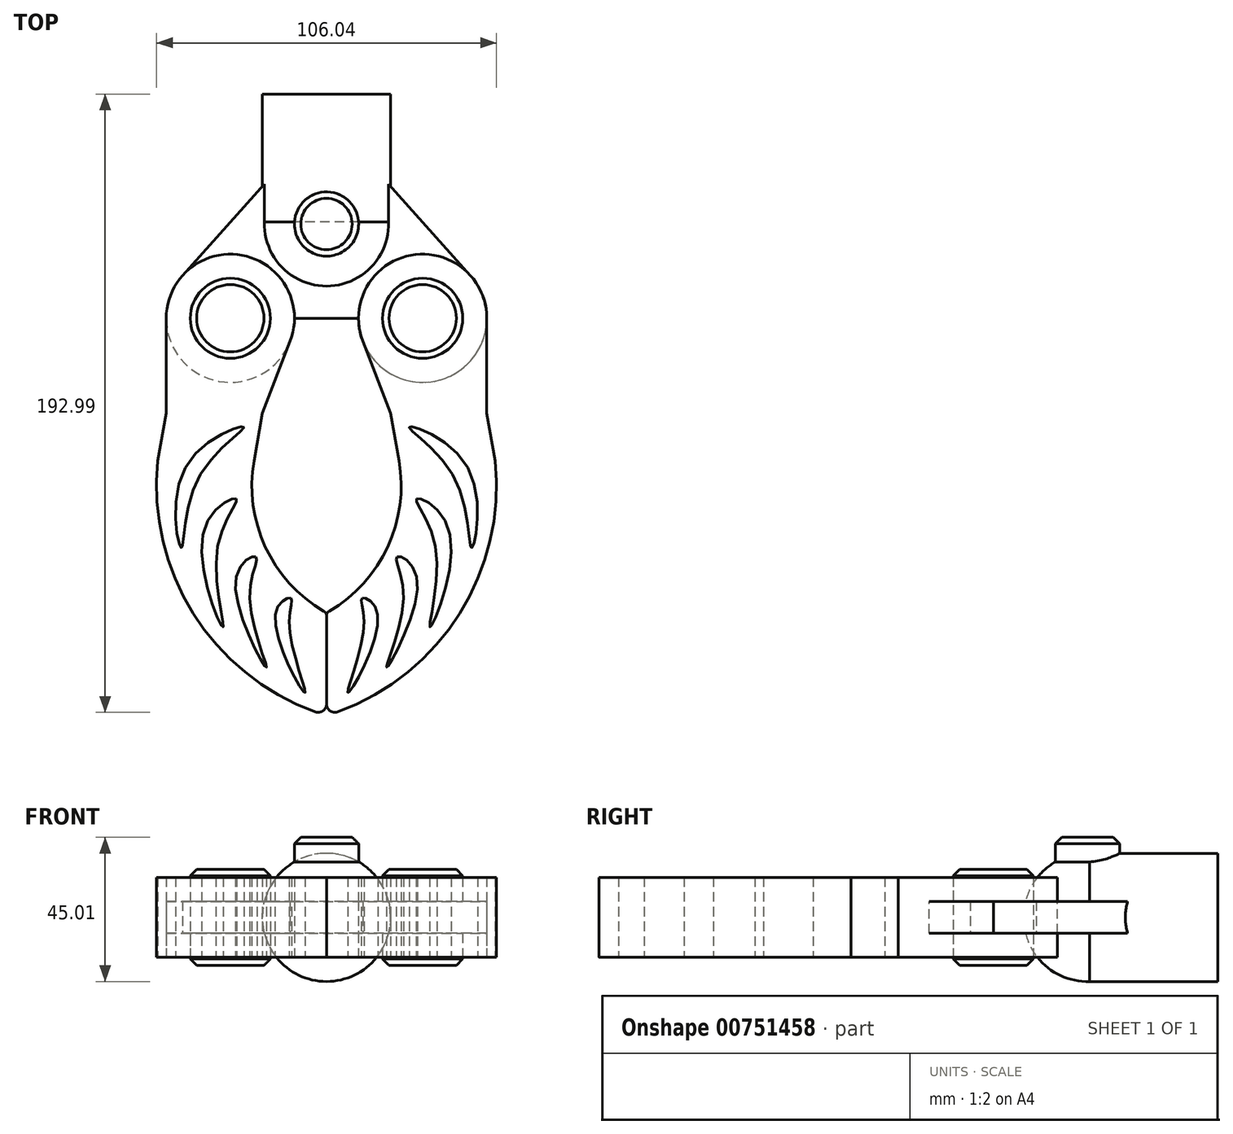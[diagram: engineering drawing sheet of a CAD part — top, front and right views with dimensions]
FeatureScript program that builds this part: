
annotation { "Feature Type Name" : "Feature", "Feature Type Description" : "" }
export const myFeature = defineFeature(function(context is Context, id is Id, definition is map)
    precondition{}
    {
        {
            var Q0;
            Q0=qCreatedBy(makeId("Top.planeOp"),FACE);
            var sketch = newSketch(context, id + "F0", { "sketchPlane" : qUnion([Q0])});
            skLineSegment(sketch, "E0", {"start": v(0, 0) * mm, "end": v(0, 30) * mm});
            skLineSegment(sketch, "E1", {"start": v(-30, 30) * mm, "end": v(-30, 20) * mm, "construction": true});
            skArc(sketch, "E2", {"start": v(-44.9, 13.33) * mm, "mid": v(-37.14, -18.68) * mm, "end": v(-10, 0) * mm});
            skLineSegment(sketch, "E3", {"start": v(-30, 30) * mm, "end": v(-44.9, 13.33) * mm});
            skLineSegment(sketch, "E4", {"start": v(0, 0) * mm, "end": v(-10, 0) * mm});
            skLineSegment(sketch, "E5", {"start": v(0, 0) * mm, "end": v(0, -500) * mm, "construction": true});
            skLineSegment(sketch, "E6", {"start": v(-30, 30) * mm, "end": v(0, 30) * mm, "construction": true});
            skCircle(sketch, "E7", {"center": v(-30, 0) * mm, "radius": 12.5 * mm, "construction": true});
            skLineSegment(sketch, "E8", {"start": v(-30, 0) * mm, "end": v(-35.2, -29.54) * mm, "construction": true});
            skArc(sketch, "E9", {"start": v(-35.2, -29.54) * mm, "mid": v(-28.67, -66.22) * mm, "end": v(0, -90) * mm, "construction": true});
            skLineSegment(sketch, "E10", {"start": v(0, -70) * mm, "end": v(0, -110) * mm});
            skArc(sketch, "E11", {"start": v(-30, 30) * mm, "mid": v(-21.21, 8.79) * mm, "end": v(0, 0) * mm, "construction": true});
            skArc(sketch, "E12", {"start": v(-10, 0) * mm, "mid": v(-22.86, 18.68) * mm, "end": v(-44.9, 13.33) * mm, "construction": true});
            skLineSegment(sketch, "E13", {"start": v(-30, 30) * mm, "end": v(0, 63.54) * mm});
            skLineSegment(sketch, "E14", {"start": v(0, 63.54) * mm, "end": v(0, 30) * mm});
            skCircle(sketch, "E15.MirrorC", {"center": v(30, 0) * mm, "radius": 12.5 * mm, "construction": true});
            skLineSegment(sketch, "E16", {"start": v(0, 70) * mm, "end": v(-20, 70) * mm, "construction": true});
            skLineSegment(sketch, "E17", {"start": v(-20, 70) * mm, "end": v(-20, 30) * mm, "construction": true});
            skArc(sketch, "E18", {"start": v(-20, 30) * mm, "mid": v(-14.14, 15.86) * mm, "end": v(0, 10) * mm, "construction": true});
            skSolve(sketch);
        }
        {
            var Q0;
            Q0=qCreatedBy(makeId("Front.planeOp"),FACE);
            var Q1;
            Q1=sQuery(id+"F0.wireOp",VERTEX,"E16.start");
            cPlane(context, id + "F1", {"entities" : qUnion([Q0, Q1]), "cplaneType" : CPlaneType.PLANE_POINT, "offset" : 25 * mm, "width" : 150 * mm, "height" : 150 * mm});
        }
        {
            var Q0;
            Q0=qCreatedBy(id+"F1.planeOp",FACE);
            var sketch = newSketch(context, id + "F2", { "sketchPlane" : qUnion([Q0])});
            skCircle(sketch, "E19", {"center": v(0, 0) * mm, "radius": 20 * mm});
            skSolve(sketch);
        }
        {
            var Q0;
            Q0=makeQuery(id+"F0.imprint","IMPRINT",FACE,{"disambiguationData":[TD([[makeQuery(id+"F0.imprint","IMPRINT",EDGE,{"derivedFrom":sQuery(id+"F0.wireOp",EDGE,"E0")}),1.0]])]});
            extrude(context, id + "F3", {"entities" : qUnion([Q0]), "endBound" : BoundingType.SYMMETRIC, "depth" : 10 * mm, "offsetDistance" : 25 * mm});
        }
        {
            var Q0;
            Q0=qCreatedBy(makeId("Top.planeOp"),FACE);
            var sketch = newSketch(context, id + "F4", { "sketchPlane" : qUnion([Q0])});
            skCircle(sketch, "E20.0", {"center": v(-30, 0) * mm, "radius": 12.5 * mm});
            skSolve(sketch);
        }
        {
            var Q0;
            Q0 = qSketchRegion(id + "F4", true);
            extrude(context, id + "F5", {"entities" : qUnion([Q0]), "operationType" : NewBodyOperationType.ADD, "endBound" : BoundingType.SYMMETRIC, "depth" : 30 * mm, "offsetDistance" : 25 * mm});
        }
        {
            var Q0;
            Q0=makeQuery(id+"F5.opExtrude","CAP_EDGE",EDGE,{"disambiguationData":[OSD([sQuery(id+"F4.wireOp",EDGE,"E20.0")])],"isStart":false});
            var Q1;
            Q1=makeQuery(id+"F5.opExtrude","CAP_EDGE",EDGE,{"disambiguationData":[OSD([sQuery(id+"F4.wireOp",EDGE,"E20.0")])],"isStart":true});
            chamfer(context, id + "F6", {"entities" : qUnion([Q0, Q1]), "width" : 2 * mm, "tangentPropagation" : true});
        }
        {
            var Q0;
            Q0=makeQuery(id+"F3.opExtrude","SWEPT_BODY",BODY,{"disambiguationData":[OSD([sQuery(id+"F0.wireOp",EDGE,"E0"),sQuery(id+"F0.wireOp",EDGE,"E2"),sQuery(id+"F0.wireOp",EDGE,"E3"),sQuery(id+"F0.wireOp",EDGE,"E4"),sQuery(id+"F0.wireOp",EDGE,"v7iHcq4s-HqqY-JVhH-IqB3-3PMgX8WB2WR8.top"),sQuery(id+"F0.wireOp",EDGE,"v7iHcq4s-HqqY-JVhH-IqB3-3PMgX8WB2WR8.left"),sQuery(id+"F0.wireOp",EDGE,"v7iHcq4s-HqqY-JVhH-IqB3-3PMgX8WB2WR8.right"),sQuery(id+"F0.wireOp",EDGE,"E6"),sQuery(id+"F0.wireOp",EDGE,"E7")])]});
            var Q1;
            Q1=makeQuery(id+"F3.opExtrude","SWEPT_FACE",FACE,{"disambiguationData":[OSD([sQuery(id+"F0.wireOp",EDGE,"E0"),sQuery(id+"F0.wireOp",EDGE,"v7iHcq4s-HqqY-JVhH-IqB3-3PMgX8WB2WR8.left")])]});
            mirror(context, id + "F7", {"operationType" : NewBodyOperationType.ADD, "entities" : qUnion([Q0]), "mirrorPlane" : qUnion([Q1])});
        }
        {
            var Q0;
            Q0=qCreatedBy(makeId("Top.planeOp"),FACE);
            var sketch = newSketch(context, id + "F8", { "sketchPlane" : qUnion([Q0])});
            skCircle(sketch, "E21", {"center": v(-30, 0) * mm, "radius": 12.5 * mm});
            skLineSegment(sketch, "E22.1", {"start": v(-20, -29.67) * mm, "end": v(-22.6, -44.44) * mm});
            skLineSegment(sketch, "E23", {"start": v(-50, -29.67) * mm, "end": v(-20, -29.67) * mm, "construction": true});
            skFitSpline(sketch, "E24", {"points": [v(-44.05, -46.6) * mm, v(-25.83, -33.95) * mm, v(-39.89, -49.73) * mm, v(-45.29, -71.66) * mm, v(-44.05, -46.6) * mm]});
            skFitSpline(sketch, "E25", {"points": [v(-22.01, -74.42) * mm, v(-24, -86.87) * mm, v(-18.8, -108.95) * mm, v(-28.27, -81.3) * mm, v(-22.01, -74.42) * mm]});
            skFitSpline(sketch, "E26", {"points": [v(-28.13, -56.31) * mm, v(-34, -71.32) * mm, v(-32.36, -96.43) * mm, v(-38.28, -66.38) * mm, v(-28.13, -56.31) * mm]});
            skArc(sketch, "E27", {"start": v(-22.6, -44.44) * mm, "mid": v(-19.09, -71.36) * mm, "end": v(-0.8, -91.42) * mm});
            skArc(sketch, "E28", {"start": v(-52.6, -44.44) * mm, "mid": v(-41.58, -92.1) * mm, "end": v(-3.5, -122.84) * mm});
            skLineSegment(sketch, "E29", {"start": v(0, -120.37) * mm, "end": v(0, -92.83) * mm});
            skLineSegment(sketch, "E30", {"start": v(-50, -29.67) * mm, "end": v(-50, 0) * mm});
            skLineSegment(sketch, "E31", {"start": v(-20, -29.67) * mm, "end": v(-11.34, -7.2) * mm});
            skArc(sketch, "E32", {"start": v(-11.34, -7.2) * mm, "mid": v(-26.34, 19.66) * mm, "end": v(-50, 0) * mm});
            skLineSegment(sketch, "E33", {"start": v(-50, -29.67) * mm, "end": v(-52.6, -44.44) * mm});
            skLineSegment(sketch, "E34", {"start": v(-52.6, -44.44) * mm, "end": v(-22.6, -44.44) * mm, "construction": true});
            skLineSegment(sketch, "E35", {"start": v(0, 0) * mm, "end": v(0, -91.88) * mm, "construction": true});
            skArc(sketch, "E36", {"start": v(-3.5, -122.84) * mm, "mid": v(-1.1, -122.5) * mm, "end": v(0, -120.33) * mm});
            skArc(sketch, "E37", {"start": v(0, -92.83) * mm, "mid": v(-0.22, -92.02) * mm, "end": v(-0.8, -91.42) * mm});
            skLineSegment(sketch, "E38.trimOffspring", {"start": v(0, -92.83) * mm, "end": v(0, -120.33) * mm, "construction": true});
            skFitSpline(sketch, "E39", {"points": [v(-11.16, -87.34) * mm, v(-11.65, -95.94) * mm, v(-6.77, -116.92) * mm, v(-15.96, -92.43) * mm, v(-11.16, -87.34) * mm]});
            skSolve(sketch);
        }
        {
            var Q0;
            Q0=makeQuery(id+"F8.imprint","IMPRINT",FACE,{"disambiguationData":[TD([[makeQuery(id+"F8.imprint","IMPRINT",EDGE,{"derivedFrom":sQuery(id+"F8.wireOp",EDGE,"E21")}),-1.0]])]});
            var Q1;
            Q1 = qConstructionFilter(qBodyType(qCreatedBy(id + "F8" ,EDGE), BodyType.WIRE), ConstructionObject.NO);
            extrude(context, id + "F9", {"entities" : qUnion([Q0]), "surfaceEntities" : qUnion([Q1]), "endBound" : BoundingType.SYMMETRIC, "depth" : 25 * mm, "offsetDistance" : 25 * mm});
        }
        {
            var Q0;
            Q0=qCreatedBy(makeId("Top.planeOp"),FACE);
            var sketch = newSketch(context, id + "F10", { "sketchPlane" : qUnion([Q0])});
            skArc(sketch, "E40.0", {"start": v(-10, 0) * mm, "mid": v(-22.86, 18.68) * mm, "end": v(-44.9, 13.33) * mm});
            skArc(sketch, "E41.0", {"start": v(-44.9, 13.33) * mm, "mid": v(-37.14, -18.68) * mm, "end": v(-10, 0) * mm});
            skCircle(sketch, "E42.0", {"center": v(-30, 0) * mm, "radius": 12.5 * mm});
            skSolve(sketch);
        }
        {
            var Q0;
            Q0 = qSketchRegion(id + "F10", true);
            extrude(context, id + "F11", {"entities" : qUnion([Q0]), "operationType" : NewBodyOperationType.REMOVE, "endBound" : BoundingType.SYMMETRIC, "oppositeDirection" : true, "depth" : 10 * mm, "offsetDistance" : 25 * mm});
        }
        {
            var Q0;
            Q0=qCreatedBy(makeId("Top.planeOp"),FACE);
            var sketch = newSketch(context, id + "F12", { "sketchPlane" : qUnion([Q0])});
            skArc(sketch, "E43", {"start": v(-20, 30) * mm, "mid": v(-14.36, 15.47) * mm, "end": v(0, 9.4) * mm});
            skLineSegment(sketch, "E44", {"start": v(-20, 30) * mm, "end": v(-20, 70) * mm});
            skLineSegment(sketch, "E45", {"start": v(-20, 70) * mm, "end": v(0, 70) * mm});
            skLineSegment(sketch, "E46", {"start": v(0, 70) * mm, "end": v(0, 9.4) * mm});
            skLineSegment(sketch, "E47", {"start": v(0, 9.4) * mm, "end": v(0, -500) * mm, "construction": true});
            skLineSegment(sketch, "E48", {"start": v(0, 9.4) * mm, "end": v(7.25, 9.4) * mm, "construction": true});
            skSolve(sketch);
        }
        {
            var Q0;
            Q0 = qSketchRegion(id + "F12", true);
            var Q1;
            Q1=sQuery(id+"F12.wireOp",EDGE,"E47");
            revolve(context, id + "F13", {"operationType" : NewBodyOperationType.ADD, "surfaceOperationType" : NewSurfaceOperationType.NEW, "entities" : qUnion([Q0]), "axis" : qUnion([Q1]), "revolveType" : RevolveType.FULL});
        }
        {
            var Q0;
            Q0=makeQuery(id+"F13.opRevolve","SWEPT_FACE",FACE,{"disambiguationData":[OSD([sQuery(id+"F12.wireOp",EDGE,"E45")])]});
            var sketch = newSketch(context, id + "F14", { "sketchPlane" : qUnion([Q0])});
            skCircle(sketch, "E49", {"center": v(0, 0) * mm, "radius": 25 * mm});
            skCircle(sketch, "E50", {"center": v(0, 0) * mm, "radius": 35 * mm});
            skSolve(sketch);
        }
        {
            var Q0;
            Q0 = qSketchRegion(id + "F14", true);
            extrude(context, id + "F15", {"entities" : qUnion([Q0]), "operationType" : NewBodyOperationType.REMOVE, "oppositeDirection" : true, "depth" : 5 * mm, "offsetDistance" : 25 * mm});
        }
        {
            var Q0;
            Q0=makeQuery(id+"F9.opExtrude","SWEPT_BODY",BODY,{"disambiguationData":[OSD([sQuery(id+"F8.wireOp",EDGE,"vaR3K8vv-5fST-HrPB-1wKU-Zu6ypuQFtfXR"),sQuery(id+"F8.wireOp",EDGE,"E21"),sQuery(id+"F8.wireOp",EDGE,"b3498736-7825-4838-836c-f4c0a6d7488f.0"),sQuery(id+"F8.wireOp",EDGE,"b3498736-7825-4838-836c-f4c0a6d7488f.1"),sQuery(id+"F8.wireOp",EDGE,"E22.0"),sQuery(id+"F8.wireOp",EDGE,"E22.1"),sQuery(id+"F8.wireOp",EDGE,"a1bgXV7K-aili-hwMm-77Qk-pOpBzdzOMLUR"),sQuery(id+"F8.wireOp",EDGE,"75008afe-1c75-47eb-afa5-69293964e4df.filletArc"),sQuery(id+"F8.wireOp",EDGE,"f4d8c7a8-47f3-4bfe-9fd1-01c12d9b734b.filletArc")])]});
            var Q1;
            Q1=qCreatedBy(makeId("Right.planeOp"),FACE);
            mirror(context, id + "F16", {"entities" : qUnion([Q0]), "mirrorPlane" : qUnion([Q1])});
        }
        {
            var Q0;
            Q0 = qSketchRegion(id + "F14", true);
            extrude(context, id + "F17", {"entities" : qUnion([Q0]), "operationType" : NewBodyOperationType.REMOVE, "oppositeDirection" : true, "depth" : 5 * mm, "offsetDistance" : 25 * mm});
        }
        {
            var Q0;
            Q0=qCreatedBy(makeId("Top.planeOp"),FACE);
            var sketch = newSketch(context, id + "F18", { "sketchPlane" : qUnion([Q0])});
            skCircle(sketch, "E51", {"center": v(0, 29.4) * mm, "radius": 10 * mm});
            skSolve(sketch);
        }
        {
            var Q0;
            Q0 = qSketchRegion(id + "F18", true);
            extrude(context, id + "F19", {"entities" : qUnion([Q0]), "operationType" : NewBodyOperationType.ADD, "depth" : 25 * mm, "offsetDistance" : 25 * mm});
        }
        {
            var Q0;
            Q0=makeQuery(id+"F19.opExtrude","CAP_EDGE",EDGE,{"disambiguationData":[OSD([sQuery(id+"F18.wireOp",EDGE,"E51")])],"isStart":false});
            chamfer(context, id + "F20", {"entities" : qUnion([Q0]), "width" : 2 * mm, "tangentPropagation" : true});
        }
    });
